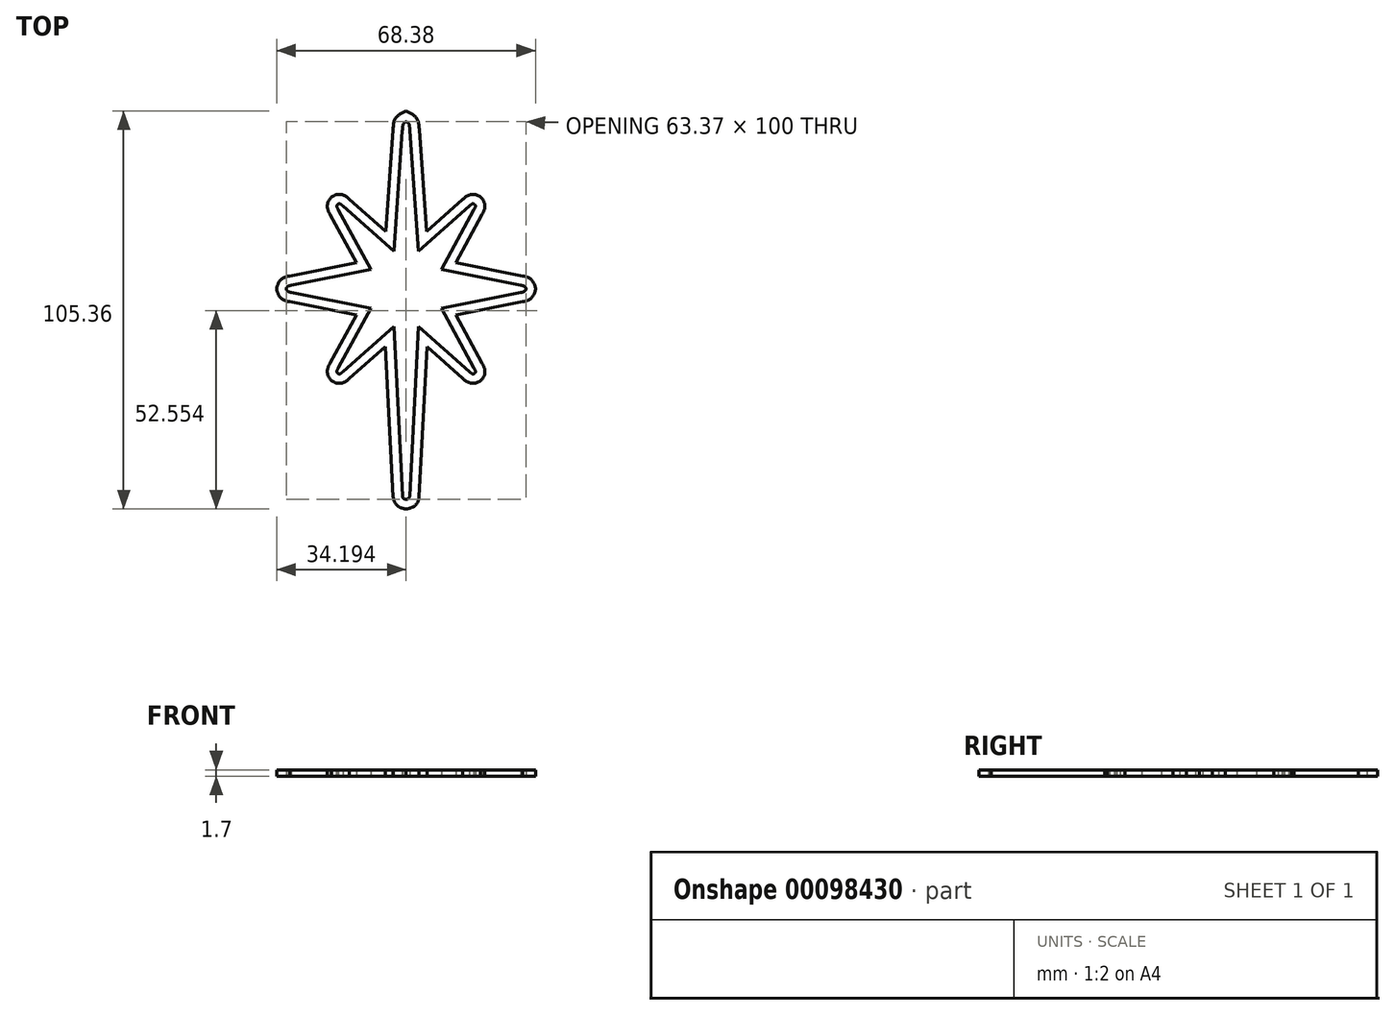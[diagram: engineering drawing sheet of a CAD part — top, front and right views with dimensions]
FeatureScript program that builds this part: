
annotation { "Feature Type Name" : "Feature", "Feature Type Description" : "" }
export const myFeature = defineFeature(function(context is Context, id is Id, definition is map)
    precondition{}
    {
        {
            var Q0;
            Q0=qCreatedBy(makeId("Top.planeOp"),FACE);
            var sketch = newSketch(context, id + "F0", { "sketchPlane" : qUnion([Q0])});
            skFitSpline(sketch, "E0", {"points": [v(-10.76, 63.05) * mm, v(-10.04, 62.48) * mm, v(-9.76, 60.62) * mm], "startDerivative": vector(2.03, -1.03) * mm, "endDerivative": vector(0.73, -6.27) * mm});
            skLineSegment(sketch, "E1", {"start": v(-9.76, 60.62) * mm, "end": v(-7.5, 28.74) * mm});
            skFitSpline(sketch, "E2.MirrorCS", {"points": [v(-10.76, 63.05) * mm, v(-11.47, 62.48) * mm, v(-11.75, 60.62) * mm], "startDerivative": vector(-2.03, -1.03) * mm, "endDerivative": vector(-0.73, -6.27) * mm});
            skLineSegment(sketch, "E3.MirrorCS", {"start": v(-11.75, 60.62) * mm, "end": v(-14.02, 28.74) * mm});
            skFitSpline(sketch, "E4", {"points": [v(-28.85, 41.13) * mm, v(-28.34, 41.28) * mm, v(-27.46, 40.63) * mm], "startDerivative": vector(1.18, 0.65) * mm, "endDerivative": vector(1.58, -1.52) * mm});
            skLineSegment(sketch, "E5", {"start": v(-27.46, 40.63) * mm, "end": v(-14.02, 28.74) * mm});
            skFitSpline(sketch, "E6.MirrorCS", {"points": [v(-28.85, 41.13) * mm, v(-29.1, 40.67) * mm, v(-28.66, 39.67) * mm], "startDerivative": vector(-0.9, -1) * mm, "endDerivative": vector(1.14, -1.88) * mm});
            skLineSegment(sketch, "E7.MirrorCS", {"start": v(-28.66, 39.67) * mm, "end": v(-20.07, 23.92) * mm});
            skPoint(sketch, "E8.orphan", {"position": v(-13.25, 20.4) * mm});
            skLineSegment(sketch, "E9.MirrorCS", {"start": v(5.95, 40.63) * mm, "end": v(-7.5, 28.74) * mm});
            skFitSpline(sketch, "E10.MirrorCS", {"points": [v(7.33, 41.13) * mm, v(6.83, 41.28) * mm, v(5.95, 40.63) * mm], "startDerivative": vector(-1.18, 0.65) * mm, "endDerivative": vector(-1.58, -1.52) * mm});
            skFitSpline(sketch, "E11.MirrorCS", {"points": [v(7.33, 41.13) * mm, v(7.59, 40.67) * mm, v(7.15, 39.67) * mm], "startDerivative": vector(0.9, -1) * mm, "endDerivative": vector(-1.14, -1.88) * mm});
            skLineSegment(sketch, "E12.MirrorCS", {"start": v(7.15, 39.67) * mm, "end": v(-1.44, 23.92) * mm});
            skLineSegment(sketch, "E13.MirrorCS", {"start": v(-28.66, -2.12) * mm, "end": v(-20.07, 13.63) * mm});
            skLineSegment(sketch, "E14.MirrorCS", {"start": v(-27.46, -3.08) * mm, "end": v(-14.02, 8.8) * mm});
            skFitSpline(sketch, "E15.MirrorCS", {"points": [v(-28.85, -3.59) * mm, v(-29.1, -3.13) * mm, v(-28.66, -2.12) * mm], "startDerivative": vector(-0.9, 1) * mm, "endDerivative": vector(1.14, 1.88) * mm});
            skLineSegment(sketch, "E16.MirrorCS", {"start": v(5.95, -3.08) * mm, "end": v(-7.5, 8.8) * mm});
            skLineSegment(sketch, "E17.MirrorCS", {"start": v(7.15, -2.12) * mm, "end": v(-1.44, 13.63) * mm});
            skFitSpline(sketch, "E18.MirrorCS", {"points": [v(7.33, -3.59) * mm, v(6.83, -3.73) * mm, v(5.95, -3.08) * mm], "startDerivative": vector(-1.18, -0.65) * mm, "endDerivative": vector(-1.58, 1.52) * mm});
            skFitSpline(sketch, "E19.MirrorCS", {"points": [v(7.33, -3.59) * mm, v(7.59, -3.13) * mm, v(7.15, -2.12) * mm], "startDerivative": vector(0.9, 1) * mm, "endDerivative": vector(-1.14, 1.88) * mm});
            skPoint(sketch, "E20.orphan", {"position": v(-7.5, 8.8) * mm});
            skFitSpline(sketch, "E21.MirrorCS", {"points": [v(-28.85, -3.59) * mm, v(-28.34, -3.73) * mm, v(-27.46, -3.08) * mm], "startDerivative": vector(1.18, -0.65) * mm, "endDerivative": vector(1.58, 1.52) * mm});
            skLineSegment(sketch, "E22", {"start": v(-20.07, 23.92) * mm, "end": v(-41.12, 19.72) * mm});
            skFitSpline(sketch, "E23", {"points": [v(-41.12, 19.72) * mm, v(-42.24, 19.26) * mm, v(-42.44, 18.77) * mm, v(-42.43, 18.77) * mm], "startDerivative": vector(-2.54, -0.48) * mm, "endDerivative": vector(0.26, 0.12) * mm});
            skLineSegment(sketch, "E24.MirrorCS", {"start": v(-20.07, 13.63) * mm, "end": v(-41.12, 17.82) * mm});
            skFitSpline(sketch, "E25.MirrorCS", {"points": [v(-41.12, 17.82) * mm, v(-42.24, 18.29) * mm, v(-42.44, 18.77) * mm, v(-42.43, 18.77) * mm], "startDerivative": vector(-2.54, 0.48) * mm, "endDerivative": vector(0.26, -0.12) * mm});
            skLineSegment(sketch, "E26.MirrorCS", {"start": v(-1.44, 23.92) * mm, "end": v(19.6, 19.72) * mm});
            skLineSegment(sketch, "E27.MirrorCS", {"start": v(-1.44, 13.63) * mm, "end": v(19.6, 17.82) * mm});
            skFitSpline(sketch, "E28.MirrorCS", {"points": [v(19.6, 17.82) * mm, v(20.73, 18.29) * mm, v(20.93, 18.77) * mm, v(20.92, 18.77) * mm], "startDerivative": vector(2.54, 0.48) * mm, "endDerivative": vector(-0.26, -0.12) * mm});
            skFitSpline(sketch, "E29.MirrorCS", {"points": [v(19.6, 19.72) * mm, v(20.73, 19.26) * mm, v(20.93, 18.77) * mm, v(20.92, 18.77) * mm], "startDerivative": vector(2.54, -0.48) * mm, "endDerivative": vector(-0.26, 0.12) * mm});
            skLineSegment(sketch, "E30", {"start": v(-14.02, 8.8) * mm, "end": v(-11.69, -36.06) * mm});
            skFitSpline(sketch, "E31", {"points": [v(-11.69, -36.06) * mm, v(-11.47, -36.67) * mm, v(-10.76, -36.95) * mm], "startDerivative": vector(0.23, -1.45) * mm, "endDerivative": vector(1.62, -0.34) * mm});
            skFitSpline(sketch, "E32.MirrorCS", {"points": [v(-9.82, -36.06) * mm, v(-10.04, -36.67) * mm, v(-10.76, -36.95) * mm], "startDerivative": vector(-0.23, -1.45) * mm, "endDerivative": vector(-1.62, -0.34) * mm});
            skLineSegment(sketch, "E33.MirrorCS", {"start": v(-7.5, 8.8) * mm, "end": v(-9.82, -36.06) * mm});
            skLineSegment(sketch, "E34", {"start": v(-10.76, 63.05) * mm, "end": v(-10.76, -36.95) * mm, "construction": true});
            skSolve(sketch);
        }
        {
            var Q0;
            Q0 = qSketchRegion(id + "F0", true);
            extrude(context, id + "F1", {"entities" : qUnion([Q0]), "depth" : 1.7 * mm});
        }
        {
            var Q0;
            Q0=makeQuery(id+"F1.opExtrude","SWEPT_BODY",BODY,{"disambiguationData":[OSD([sQuery(id+"F0.wireOp",EDGE,"E0"),sQuery(id+"F0.wireOp",EDGE,"E1"),sQuery(id+"F0.wireOp",EDGE,"E2.MirrorCS"),sQuery(id+"F0.wireOp",EDGE,"E3.MirrorCS"),sQuery(id+"F0.wireOp",EDGE,"E4"),sQuery(id+"F0.wireOp",EDGE,"E5"),sQuery(id+"F0.wireOp",EDGE,"E6.MirrorCS"),sQuery(id+"F0.wireOp",EDGE,"E7.MirrorCS"),sQuery(id+"F0.wireOp",EDGE,"E9.MirrorCS"),sQuery(id+"F0.wireOp",EDGE,"E10.MirrorCS"),sQuery(id+"F0.wireOp",EDGE,"E11.MirrorCS"),sQuery(id+"F0.wireOp",EDGE,"E12.MirrorCS"),sQuery(id+"F0.wireOp",EDGE,"E13.MirrorCS"),sQuery(id+"F0.wireOp",EDGE,"E14.MirrorCS"),sQuery(id+"F0.wireOp",EDGE,"E15.MirrorCS"),sQuery(id+"F0.wireOp",EDGE,"E16.MirrorCS"),sQuery(id+"F0.wireOp",EDGE,"E17.MirrorCS"),sQuery(id+"F0.wireOp",EDGE,"E18.MirrorCS"),sQuery(id+"F0.wireOp",EDGE,"E19.MirrorCS"),sQuery(id+"F0.wireOp",EDGE,"E21.MirrorCS"),sQuery(id+"F0.wireOp",EDGE,"E22"),sQuery(id+"F0.wireOp",EDGE,"E23"),sQuery(id+"F0.wireOp",EDGE,"E24.MirrorCS"),sQuery(id+"F0.wireOp",EDGE,"E25.MirrorCS"),sQuery(id+"F0.wireOp",EDGE,"E26.MirrorCS"),sQuery(id+"F0.wireOp",EDGE,"E27.MirrorCS"),sQuery(id+"F0.wireOp",EDGE,"E28.MirrorCS"),sQuery(id+"F0.wireOp",EDGE,"E29.MirrorCS"),sQuery(id+"F0.wireOp",EDGE,"E30"),sQuery(id+"F0.wireOp",EDGE,"E31"),sQuery(id+"F0.wireOp",EDGE,"E32.MirrorCS"),sQuery(id+"F0.wireOp",EDGE,"E33.MirrorCS")])]});
            transform(context, id + "F2", {"entities" : qUnion([Q0]), "transformType" : TransformType.TRANSLATION_3D, "dx" : 0 * mm, "dy" : 0 * mm, "dz" : 0 * mm, "makeCopy" : true});
        }
        {
            var Q0;
            Q0=makeQuery(id+"F1.opExtrude","CAP_FACE",FACE,{"disambiguationData":[OSD([sQuery(id+"F0.wireOp",EDGE,"E0"),sQuery(id+"F0.wireOp",EDGE,"E1"),sQuery(id+"F0.wireOp",EDGE,"E2.MirrorCS"),sQuery(id+"F0.wireOp",EDGE,"E3.MirrorCS"),sQuery(id+"F0.wireOp",EDGE,"E4"),sQuery(id+"F0.wireOp",EDGE,"E5"),sQuery(id+"F0.wireOp",EDGE,"E6.MirrorCS"),sQuery(id+"F0.wireOp",EDGE,"E7.MirrorCS"),sQuery(id+"F0.wireOp",EDGE,"E9.MirrorCS"),sQuery(id+"F0.wireOp",EDGE,"E10.MirrorCS"),sQuery(id+"F0.wireOp",EDGE,"E11.MirrorCS"),sQuery(id+"F0.wireOp",EDGE,"E12.MirrorCS"),sQuery(id+"F0.wireOp",EDGE,"E13.MirrorCS"),sQuery(id+"F0.wireOp",EDGE,"E14.MirrorCS"),sQuery(id+"F0.wireOp",EDGE,"E15.MirrorCS"),sQuery(id+"F0.wireOp",EDGE,"E16.MirrorCS"),sQuery(id+"F0.wireOp",EDGE,"E17.MirrorCS"),sQuery(id+"F0.wireOp",EDGE,"E18.MirrorCS"),sQuery(id+"F0.wireOp",EDGE,"E19.MirrorCS"),sQuery(id+"F0.wireOp",EDGE,"E21.MirrorCS"),sQuery(id+"F0.wireOp",EDGE,"E22"),sQuery(id+"F0.wireOp",EDGE,"E23"),sQuery(id+"F0.wireOp",EDGE,"E24.MirrorCS"),sQuery(id+"F0.wireOp",EDGE,"E25.MirrorCS"),sQuery(id+"F0.wireOp",EDGE,"E26.MirrorCS"),sQuery(id+"F0.wireOp",EDGE,"E27.MirrorCS"),sQuery(id+"F0.wireOp",EDGE,"E28.MirrorCS"),sQuery(id+"F0.wireOp",EDGE,"E29.MirrorCS"),sQuery(id+"F0.wireOp",EDGE,"E30"),sQuery(id+"F0.wireOp",EDGE,"E31"),sQuery(id+"F0.wireOp",EDGE,"E32.MirrorCS"),sQuery(id+"F0.wireOp",EDGE,"E33.MirrorCS")])],"isStart":false});
            var Q1;
            Q1=makeQuery(id+"F1.opExtrude","CAP_FACE",FACE,{"disambiguationData":[OSD([sQuery(id+"F0.wireOp",EDGE,"E0"),sQuery(id+"F0.wireOp",EDGE,"E1"),sQuery(id+"F0.wireOp",EDGE,"E2.MirrorCS"),sQuery(id+"F0.wireOp",EDGE,"E3.MirrorCS"),sQuery(id+"F0.wireOp",EDGE,"E4"),sQuery(id+"F0.wireOp",EDGE,"E5"),sQuery(id+"F0.wireOp",EDGE,"E6.MirrorCS"),sQuery(id+"F0.wireOp",EDGE,"E7.MirrorCS"),sQuery(id+"F0.wireOp",EDGE,"E9.MirrorCS"),sQuery(id+"F0.wireOp",EDGE,"E10.MirrorCS"),sQuery(id+"F0.wireOp",EDGE,"E11.MirrorCS"),sQuery(id+"F0.wireOp",EDGE,"E12.MirrorCS"),sQuery(id+"F0.wireOp",EDGE,"E13.MirrorCS"),sQuery(id+"F0.wireOp",EDGE,"E14.MirrorCS"),sQuery(id+"F0.wireOp",EDGE,"E15.MirrorCS"),sQuery(id+"F0.wireOp",EDGE,"E16.MirrorCS"),sQuery(id+"F0.wireOp",EDGE,"E17.MirrorCS"),sQuery(id+"F0.wireOp",EDGE,"E18.MirrorCS"),sQuery(id+"F0.wireOp",EDGE,"E19.MirrorCS"),sQuery(id+"F0.wireOp",EDGE,"E21.MirrorCS"),sQuery(id+"F0.wireOp",EDGE,"E22"),sQuery(id+"F0.wireOp",EDGE,"E23"),sQuery(id+"F0.wireOp",EDGE,"E24.MirrorCS"),sQuery(id+"F0.wireOp",EDGE,"E25.MirrorCS"),sQuery(id+"F0.wireOp",EDGE,"E26.MirrorCS"),sQuery(id+"F0.wireOp",EDGE,"E27.MirrorCS"),sQuery(id+"F0.wireOp",EDGE,"E28.MirrorCS"),sQuery(id+"F0.wireOp",EDGE,"E29.MirrorCS"),sQuery(id+"F0.wireOp",EDGE,"E30"),sQuery(id+"F0.wireOp",EDGE,"E31"),sQuery(id+"F0.wireOp",EDGE,"E32.MirrorCS"),sQuery(id+"F0.wireOp",EDGE,"E33.MirrorCS")])],"isStart":true});
            shell(context, id + "F3", {"entities" : qUnion([Q0, Q1]), "thickness" : 2.5 * mm, "oppositeDirection" : true});
        }
    });
